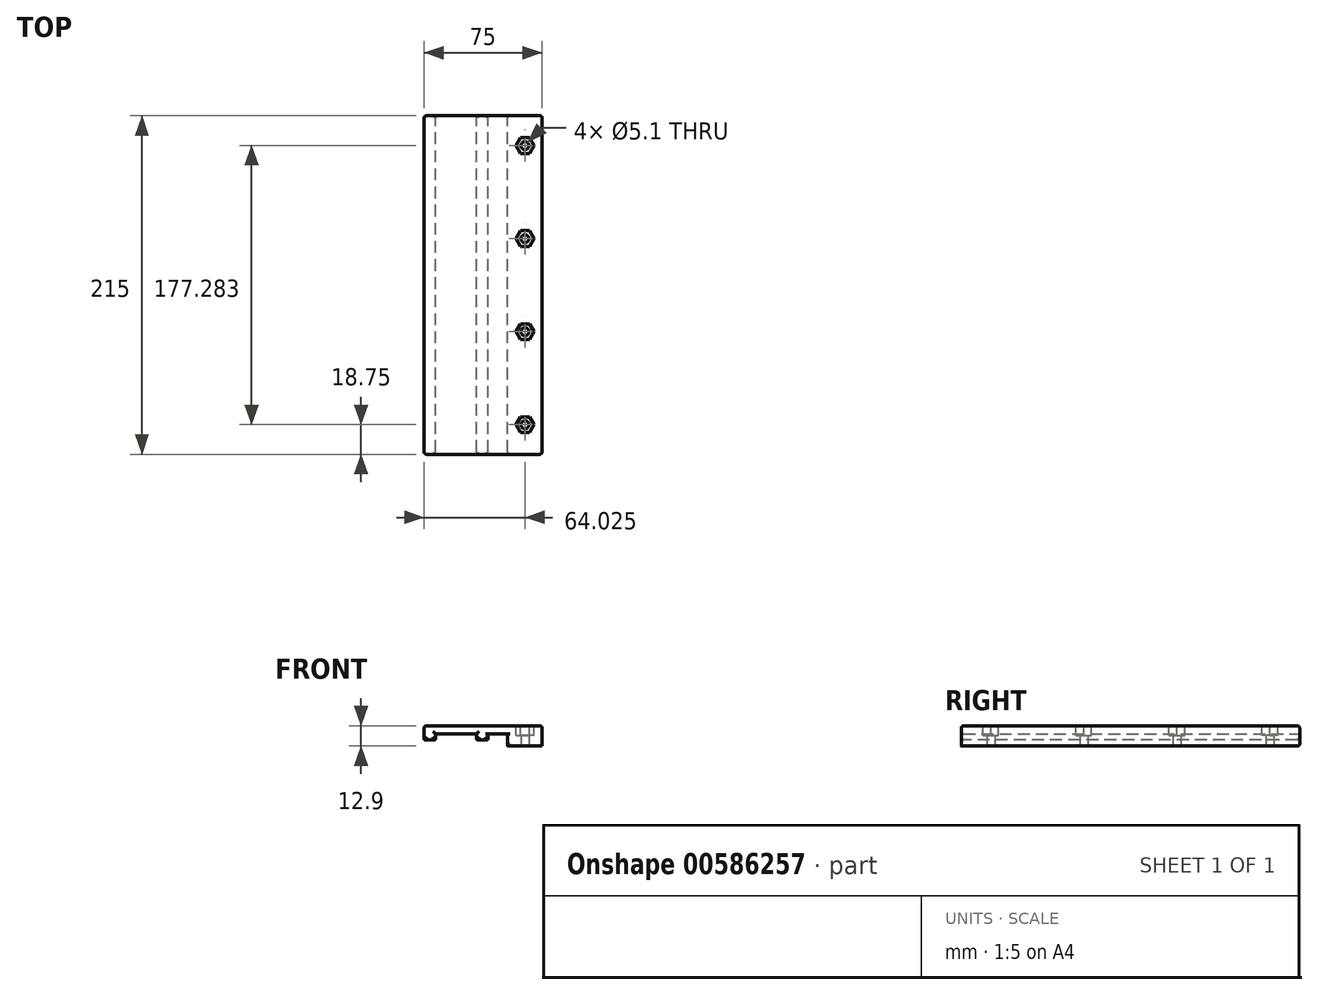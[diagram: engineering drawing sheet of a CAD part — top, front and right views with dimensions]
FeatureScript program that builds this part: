
annotation { "Feature Type Name" : "Feature", "Feature Type Description" : "" }
export const myFeature = defineFeature(function(context is Context, id is Id, definition is map)
    precondition{}
    {
        {
            var Q0;
            Q0=qCreatedBy(makeId("Top.planeOp"),FACE);
            var sketch = newSketch(context, id + "F0", { "sketchPlane" : qUnion([Q0])});
            skLineSegment(sketch, "E0.bottom", {"start": v(37.5, 107.5) * mm, "end": v(-37.5, 107.5) * mm});
            skLineSegment(sketch, "E0.top", {"start": v(37.5, -107.5) * mm, "end": v(-37.5, -107.5) * mm});
            skLineSegment(sketch, "E0.left", {"start": v(37.5, 107.5) * mm, "end": v(37.5, -107.5) * mm});
            skLineSegment(sketch, "E0.right", {"start": v(-37.5, 107.5) * mm, "end": v(-37.5, -107.5) * mm});
            skPoint(sketch, "E0.middle", {"position": v(0, 0) * mm});
            skSolve(sketch);
        }
        {
            var Q0;
            Q0=makeQuery(id+"F0.imprint","IMPRINT",FACE,{"disambiguationData":[TD([[makeQuery(id+"F0.imprint","IMPRINT",EDGE,{"derivedFrom":sQuery(id+"F0.wireOp",EDGE,"E0.bottom")}),1.0]])]});
            extrude(context, id + "F1", {"entities" : qUnion([Q0]), "depth" : 5 * mm, "offsetDistance" : 25 * mm});
        }
        {
            var Q0;
            Q0=makeQuery(id+"F1.opExtrude","CAP_FACE",FACE,{"disambiguationData":[OSD([sQuery(id+"F0.wireOp",EDGE,"E0.bottom"),sQuery(id+"F0.wireOp",EDGE,"E0.top"),sQuery(id+"F0.wireOp",EDGE,"E0.left"),sQuery(id+"F0.wireOp",EDGE,"E0.right")])],"isStart":true});
            var sketch = newSketch(context, id + "F2", { "sketchPlane" : qUnion([Q0])});
            skLineSegment(sketch, "E1.bottom", {"start": v(-37.5, 107.5) * mm, "end": v(-30.3, 107.5) * mm});
            skLineSegment(sketch, "E1.top", {"start": v(-37.5, -107.5) * mm, "end": v(-30.3, -107.5) * mm});
            skLineSegment(sketch, "E1.left", {"start": v(-37.5, 107.5) * mm, "end": v(-37.5, -107.5) * mm});
            skLineSegment(sketch, "E1.right", {"start": v(-30.3, 107.5) * mm, "end": v(-30.3, -107.5) * mm});
            skLineSegment(sketch, "E2.bottom", {"start": v(-4.15, 107.5) * mm, "end": v(3.05, 107.5) * mm});
            skLineSegment(sketch, "E2.top", {"start": v(-4.15, -107.5) * mm, "end": v(3.05, -107.5) * mm});
            skLineSegment(sketch, "E2.left", {"start": v(-4.15, 107.5) * mm, "end": v(-4.15, -107.5) * mm});
            skLineSegment(sketch, "E2.right", {"start": v(3.05, 107.5) * mm, "end": v(3.05, -107.5) * mm});
            skSolve(sketch);
        }
        {
            var Q0;
            Q0=makeQuery(id+"F2.imprint","IMPRINT",FACE,{"disambiguationData":[TD([[makeQuery(id+"F2.imprint","IMPRINT",EDGE,{"derivedFrom":sQuery(id+"F2.wireOp",EDGE,"E1.bottom")}),1.0]])]});
            var Q1;
            Q1=makeQuery(id+"F2.imprint","IMPRINT",FACE,{"disambiguationData":[TD([[makeQuery(id+"F2.imprint","IMPRINT",EDGE,{"derivedFrom":sQuery(id+"F2.wireOp",EDGE,"E2.bottom")}),1.0]])]});
            extrude(context, id + "F3", {"entities" : qUnion([Q0, Q1]), "operationType" : NewBodyOperationType.ADD, "depth" : 4 * mm, "offsetDistance" : 25 * mm});
        }
        {
            var Q0;
            {var subQ0=sQuery(id+"F0.wireOp",EDGE,"E0.left");var subQ1=sQuery(id+"F0.wireOp",EDGE,"E0.top");var subQ2=sQuery(id+"F0.wireOp",EDGE,"E0.bottom");Q0=makeQuery(id+"F3.boolean.opBoolean","SPLIT",FACE,{"disambiguationData":[TD([makeQuery(id+"F1.opExtrude","SWEPT_FACE",FACE,{"disambiguationData":[OSD([subQ0])]})])],"derivedFrom":makeQuery(id+"F1.opExtrude","CAP_FACE",FACE,{"disambiguationData":[OSD([subQ2,subQ1,subQ0,sQuery(id+"F0.wireOp",EDGE,"E0.right")])],"isStart":true})});}
            var sketch = newSketch(context, id + "F4", { "sketchPlane" : qUnion([Q0])});
            skLineSegment(sketch, "E3.bottom", {"start": v(37.5, 107.5) * mm, "end": v(15.55, 107.5) * mm});
            skLineSegment(sketch, "E3.top", {"start": v(37.5, -107.5) * mm, "end": v(15.55, -107.5) * mm});
            skLineSegment(sketch, "E3.left", {"start": v(37.5, 107.5) * mm, "end": v(37.5, -107.5) * mm});
            skLineSegment(sketch, "E3.right", {"start": v(15.55, 107.5) * mm, "end": v(15.55, -107.5) * mm});
            skSolve(sketch);
        }
        {
            var Q0;
            Q0=makeQuery(id+"F4.imprint","IMPRINT",FACE,{"disambiguationData":[TD([[makeQuery(id+"F4.imprint","IMPRINT",EDGE,{"derivedFrom":sQuery(id+"F4.wireOp",EDGE,"E3.bottom")}),1.0]])]});
            extrude(context, id + "F5", {"entities" : qUnion([Q0]), "operationType" : NewBodyOperationType.ADD, "depth" : 7.9 * mm, "offsetDistance" : 25 * mm});
        }
        {
            var Q0;
            Q0=makeQuery(id+"F5.opExtrude","CAP_FACE",FACE,{"disambiguationData":[OSD([sQuery(id+"F4.wireOp",EDGE,"E3.bottom"),sQuery(id+"F4.wireOp",EDGE,"E3.top"),sQuery(id+"F4.wireOp",EDGE,"E3.left"),sQuery(id+"F4.wireOp",EDGE,"E3.right")])],"isStart":false});
            var sketch = newSketch(context, id + "F6", { "sketchPlane" : qUnion([Q0])});
            skCircle(sketch, "E4", {"center": v(26.53, 88.75) * mm, "radius": 2.55 * mm});
            skCircle(sketch, "E5", {"center": v(26.53, 29.66) * mm, "radius": 2.55 * mm});
            skCircle(sketch, "E6", {"center": v(26.53, -29.44) * mm, "radius": 2.55 * mm});
            skCircle(sketch, "E7", {"center": v(26.53, -88.53) * mm, "radius": 2.55 * mm});
            skPoint(sketch, "E8", {"position": v(26.53, 107.5) * mm});
            skPoint(sketch, "E9", {"position": v(26.53, -107.5) * mm});
            skLineSegment(sketch, "E10", {"start": v(26.53, 107.5) * mm, "end": v(26.53, 88.75) * mm, "construction": true});
            skLineSegment(sketch, "E11", {"start": v(26.53, 88.75) * mm, "end": v(26.53, 29.66) * mm, "construction": true});
            skLineSegment(sketch, "E12", {"start": v(26.53, 29.66) * mm, "end": v(26.53, -29.44) * mm, "construction": true});
            skLineSegment(sketch, "E13", {"start": v(26.53, -29.44) * mm, "end": v(26.53, -88.53) * mm, "construction": true});
            skLineSegment(sketch, "E14", {"start": v(26.53, -88.53) * mm, "end": v(26.53, -107.5) * mm, "construction": true});
            skSolve(sketch);
        }
        {
            var Q0;
            Q0=makeQuery(id+"F6.imprint","IMPRINT",FACE,{"disambiguationData":[TD([[makeQuery(id+"F6.imprint","IMPRINT",EDGE,{"derivedFrom":sQuery(id+"F6.wireOp",EDGE,"E4")}),1.0]])]});
            var Q1;
            Q1=makeQuery(id+"F6.imprint","IMPRINT",FACE,{"disambiguationData":[TD([[makeQuery(id+"F6.imprint","IMPRINT",EDGE,{"derivedFrom":sQuery(id+"F6.wireOp",EDGE,"E5")}),1.0]])]});
            var Q2;
            Q2=makeQuery(id+"F6.imprint","IMPRINT",FACE,{"disambiguationData":[TD([[makeQuery(id+"F6.imprint","IMPRINT",EDGE,{"derivedFrom":sQuery(id+"F6.wireOp",EDGE,"E6")}),1.0]])]});
            var Q3;
            Q3=makeQuery(id+"F6.imprint","IMPRINT",FACE,{"disambiguationData":[TD([[makeQuery(id+"F6.imprint","IMPRINT",EDGE,{"derivedFrom":sQuery(id+"F6.wireOp",EDGE,"E7")}),1.0]])]});
            var Q4;
            Q4=makeQuery(id+"F1.opExtrude","CAP_FACE",FACE,{"disambiguationData":[OSD([sQuery(id+"F0.wireOp",EDGE,"E0.bottom"),sQuery(id+"F0.wireOp",EDGE,"E0.top"),sQuery(id+"F0.wireOp",EDGE,"E0.left"),sQuery(id+"F0.wireOp",EDGE,"E0.right")])],"isStart":false});
            extrude(context, id + "F7", {"entities" : qUnion([Q0, Q1, Q2, Q3]), "operationType" : NewBodyOperationType.REMOVE, "endBound" : BoundingType.UP_TO_SURFACE, "oppositeDirection" : true, "depth" : 25 * mm, "endBoundEntityFace" : qUnion([Q4]), "offsetDistance" : 25 * mm});
        }
        {
            var Q0;
            Q0=makeQuery(id+"F3.opExtrude","SWEPT_EDGE",EDGE,{"disambiguationData":[OSD([sQuery(id+"F0.wireOp",EDGE,"E0.bottom"),sQuery(id+"F2.wireOp",EDGE,"E1.top"),sQuery(id+"F2.wireOp",EDGE,"E1.right")])]});
            var Q1;
            Q1=makeQuery(id+"F3.opExtrude","CAP_EDGE",EDGE,{"disambiguationData":[OSD([sQuery(id+"F2.wireOp",EDGE,"E1.top")])],"isStart":false});
            var Q2;
            Q2=makeQuery(id+"F3.boolean.opBoolean","MERGE",EDGE,{"derivedFrom":[makeQuery(id+"F1.opExtrude","SWEPT_EDGE",EDGE,{"disambiguationData":[OSD([sQuery(id+"F0.wireOp",EDGE,"E0.bottom"),sQuery(id+"F0.wireOp",EDGE,"E0.right")])]}),makeQuery(id+"F3.opExtrude","SWEPT_EDGE",EDGE,{"disambiguationData":[OSD([sQuery(id+"F2.wireOp",EDGE,"E1.top"),sQuery(id+"F2.wireOp",EDGE,"E1.left")])]})]});
            var Q3;
            Q3=makeQuery(id+"F3.opExtrude","SWEPT_EDGE",EDGE,{"disambiguationData":[OSD([sQuery(id+"F0.wireOp",EDGE,"E0.bottom"),sQuery(id+"F2.wireOp",EDGE,"E2.top"),sQuery(id+"F2.wireOp",EDGE,"E2.left")])]});
            var Q4;
            Q4=makeQuery(id+"F3.opExtrude","CAP_EDGE",EDGE,{"disambiguationData":[OSD([sQuery(id+"F2.wireOp",EDGE,"E2.top")])],"isStart":false});
            var Q5;
            Q5=makeQuery(id+"F3.opExtrude","SWEPT_EDGE",EDGE,{"disambiguationData":[OSD([sQuery(id+"F0.wireOp",EDGE,"E0.bottom"),sQuery(id+"F2.wireOp",EDGE,"E2.top"),sQuery(id+"F2.wireOp",EDGE,"E2.right")])]});
            var Q6;
            Q6=makeQuery(id+"F5.opExtrude","SWEPT_EDGE",EDGE,{"disambiguationData":[OSD([sQuery(id+"F0.wireOp",EDGE,"E0.bottom"),sQuery(id+"F4.wireOp",EDGE,"E3.top"),sQuery(id+"F4.wireOp",EDGE,"E3.right")])]});
            var Q7;
            Q7=makeQuery(id+"F5.boolean.opBoolean","MERGE",EDGE,{"derivedFrom":[makeQuery(id+"F1.opExtrude","SWEPT_EDGE",EDGE,{"disambiguationData":[OSD([sQuery(id+"F0.wireOp",EDGE,"E0.bottom"),sQuery(id+"F0.wireOp",EDGE,"E0.left")])]}),makeQuery(id+"F5.opExtrude","SWEPT_EDGE",EDGE,{"disambiguationData":[OSD([sQuery(id+"F4.wireOp",EDGE,"E3.top"),sQuery(id+"F4.wireOp",EDGE,"E3.left")])]})]});
            var Q8;
            Q8=makeQuery(id+"F5.opExtrude","CAP_EDGE",EDGE,{"disambiguationData":[OSD([sQuery(id+"F4.wireOp",EDGE,"E3.top")])],"isStart":false});
            var Q9;
            Q9=makeQuery(id+"F5.opExtrude","SWEPT_EDGE",EDGE,{"disambiguationData":[OSD([sQuery(id+"F0.wireOp",EDGE,"E0.top"),sQuery(id+"F4.wireOp",EDGE,"E3.bottom"),sQuery(id+"F4.wireOp",EDGE,"E3.right")])]});
            var Q10;
            Q10=makeQuery(id+"F3.opExtrude","SWEPT_EDGE",EDGE,{"disambiguationData":[OSD([sQuery(id+"F0.wireOp",EDGE,"E0.top"),sQuery(id+"F2.wireOp",EDGE,"E2.bottom"),sQuery(id+"F2.wireOp",EDGE,"E2.right")])]});
            var Q11;
            Q11=makeQuery(id+"F3.opExtrude","SWEPT_EDGE",EDGE,{"disambiguationData":[OSD([sQuery(id+"F0.wireOp",EDGE,"E0.top"),sQuery(id+"F2.wireOp",EDGE,"E2.bottom"),sQuery(id+"F2.wireOp",EDGE,"E2.left")])]});
            var Q12;
            Q12=makeQuery(id+"F3.opExtrude","SWEPT_EDGE",EDGE,{"disambiguationData":[OSD([sQuery(id+"F0.wireOp",EDGE,"E0.top"),sQuery(id+"F2.wireOp",EDGE,"E1.bottom"),sQuery(id+"F2.wireOp",EDGE,"E1.right")])]});
            var Q13;
            {var subQ0=sQuery(id+"F0.wireOp",EDGE,"E0.top");Q13=makeQuery(id+"F3.boolean.opBoolean","SPLIT",EDGE,{"disambiguationData":[TD([makeQuery(id+"F3.opExtrude","SWEPT_FACE",FACE,{"disambiguationData":[OSD([sQuery(id+"F2.wireOp",EDGE,"E1.right")])]})])],"derivedFrom":makeQuery(id+"F1.opExtrude","CAP_EDGE",EDGE,{"disambiguationData":[OSD([subQ0])],"isStart":true})});}
            var Q14;
            Q14=makeQuery(id+"F3.boolean.opBoolean","MERGE",EDGE,{"derivedFrom":[makeQuery(id+"F1.opExtrude","SWEPT_EDGE",EDGE,{"disambiguationData":[OSD([sQuery(id+"F0.wireOp",EDGE,"E0.top"),sQuery(id+"F0.wireOp",EDGE,"E0.right")])]}),makeQuery(id+"F3.opExtrude","SWEPT_EDGE",EDGE,{"disambiguationData":[OSD([sQuery(id+"F2.wireOp",EDGE,"E1.bottom"),sQuery(id+"F2.wireOp",EDGE,"E1.left")])]})]});
            var Q15;
            Q15=makeQuery(id+"F3.opExtrude","CAP_EDGE",EDGE,{"disambiguationData":[OSD([sQuery(id+"F2.wireOp",EDGE,"E2.bottom")])],"isStart":false});
            var Q16;
            Q16=makeQuery(id+"F3.opExtrude","CAP_EDGE",EDGE,{"disambiguationData":[OSD([sQuery(id+"F2.wireOp",EDGE,"E1.bottom")])],"isStart":false});
            var Q17;
            Q17=makeQuery(id+"F1.opExtrude","CAP_EDGE",EDGE,{"disambiguationData":[OSD([sQuery(id+"F0.wireOp",EDGE,"E0.left")])],"isStart":false});
            var Q18;
            Q18=makeQuery(id+"F1.opExtrude","CAP_EDGE",EDGE,{"disambiguationData":[OSD([sQuery(id+"F0.wireOp",EDGE,"E0.right")])],"isStart":false});
            var Q19;
            Q19=makeQuery(id+"F1.opExtrude","CAP_EDGE",EDGE,{"disambiguationData":[OSD([sQuery(id+"F0.wireOp",EDGE,"E0.bottom")])],"isStart":false});
            var Q20;
            Q20=makeQuery(id+"F1.opExtrude","CAP_EDGE",EDGE,{"disambiguationData":[OSD([sQuery(id+"F0.wireOp",EDGE,"E0.top")])],"isStart":false});
            var Q21;
            Q21=makeQuery(id+"F5.boolean.opBoolean","MERGE",EDGE,{"derivedFrom":[makeQuery(id+"F1.opExtrude","SWEPT_EDGE",EDGE,{"disambiguationData":[OSD([sQuery(id+"F0.wireOp",EDGE,"E0.top"),sQuery(id+"F0.wireOp",EDGE,"E0.left")])]}),makeQuery(id+"F5.opExtrude","SWEPT_EDGE",EDGE,{"disambiguationData":[OSD([sQuery(id+"F4.wireOp",EDGE,"E3.bottom"),sQuery(id+"F4.wireOp",EDGE,"E3.left")])]})]});
            fillet(context, id + "F8", {"entities" : qUnion([Q0, Q1, Q2, Q3, Q4, Q5, Q6, Q7, Q8, Q9, Q10, Q11, Q12, Q13, Q14, Q15, Q16, Q17, Q18, Q19, Q20, Q21]), "radius" : 1.5 * mm, "tangentPropagation" : true, "allowEdgeOverflow" : false});
        }
        {
            var Q0;
            Q0=makeQuery(id+"F3.opExtrude","CAP_EDGE",EDGE,{"disambiguationData":[OSD([sQuery(id+"F2.wireOp",EDGE,"E1.right")])],"isStart":false});
            var Q1;
            Q1=makeQuery(id+"F3.opExtrude","CAP_EDGE",EDGE,{"disambiguationData":[OSD([sQuery(id+"F2.wireOp",EDGE,"E2.left")])],"isStart":false});
            var Q2;
            Q2=makeQuery(id+"F3.opExtrude","CAP_EDGE",EDGE,{"disambiguationData":[OSD([sQuery(id+"F2.wireOp",EDGE,"E2.right")])],"isStart":false});
            var Q3;
            Q3=makeQuery(id+"F3.opExtrude","CAP_EDGE",EDGE,{"disambiguationData":[OSD([sQuery(id+"F2.wireOp",EDGE,"E1.left")])],"isStart":false});
            fillet(context, id + "F9", {"entities" : qUnion([Q0, Q1, Q2, Q3]), "radius" : .7 * mm, "tangentPropagation" : true, "allowEdgeOverflow" : false});
        }
        {
            var Q0;
            Q0=makeQuery(id+"F1.opExtrude","CAP_FACE",FACE,{"disambiguationData":[OSD([sQuery(id+"F0.wireOp",EDGE,"E0.bottom"),sQuery(id+"F0.wireOp",EDGE,"E0.top"),sQuery(id+"F0.wireOp",EDGE,"E0.left"),sQuery(id+"F0.wireOp",EDGE,"E0.right")])],"isStart":false});
            var sketch = newSketch(context, id + "F10", { "sketchPlane" : qUnion([Q0])});
            skCircle(sketch, "E15.cCircle", {"center": v(26.53, 88.53) * mm, "radius": 5 * mm, "construction": true});
            skLineSegment(sketch, "E15.0", {"start": v(29.41, 83.53) * mm, "end": v(23.64, 83.53) * mm});
            skLineSegment(sketch, "E15.1", {"start": v(23.64, 83.53) * mm, "end": v(20.75, 88.53) * mm});
            skLineSegment(sketch, "E15.2", {"start": v(20.75, 88.53) * mm, "end": v(23.64, 93.53) * mm});
            skLineSegment(sketch, "E15.3", {"start": v(23.64, 93.53) * mm, "end": v(29.41, 93.53) * mm});
            skLineSegment(sketch, "E15.4", {"start": v(29.41, 93.53) * mm, "end": v(32.3, 88.53) * mm});
            skLineSegment(sketch, "E15.5", {"start": v(32.3, 88.53) * mm, "end": v(29.41, 83.53) * mm});
            skPoint(sketch, "E15.0.midPoint", {"position": v(26.53, 83.53) * mm});
            skCircle(sketch, "E16.cCircle", {"center": v(26.53, 29.44) * mm, "radius": 5 * mm, "construction": true});
            skLineSegment(sketch, "E16.0", {"start": v(23.64, 34.44) * mm, "end": v(29.41, 34.44) * mm});
            skLineSegment(sketch, "E16.1", {"start": v(29.41, 34.44) * mm, "end": v(32.3, 29.44) * mm});
            skLineSegment(sketch, "E16.2", {"start": v(32.3, 29.44) * mm, "end": v(29.41, 24.44) * mm});
            skLineSegment(sketch, "E16.3", {"start": v(29.41, 24.44) * mm, "end": v(23.64, 24.44) * mm});
            skLineSegment(sketch, "E16.4", {"start": v(23.64, 24.44) * mm, "end": v(20.75, 29.44) * mm});
            skLineSegment(sketch, "E16.5", {"start": v(20.75, 29.44) * mm, "end": v(23.64, 34.44) * mm});
            skPoint(sketch, "E16.0.midPoint", {"position": v(26.53, 34.44) * mm});
            skCircle(sketch, "E17.cCircle", {"center": v(26.53, -29.66) * mm, "radius": 5 * mm, "construction": true});
            skLineSegment(sketch, "E17.0", {"start": v(23.64, -24.66) * mm, "end": v(29.41, -24.66) * mm});
            skLineSegment(sketch, "E17.1", {"start": v(29.41, -24.66) * mm, "end": v(32.3, -29.66) * mm});
            skLineSegment(sketch, "E17.2", {"start": v(32.3, -29.66) * mm, "end": v(29.41, -34.66) * mm});
            skLineSegment(sketch, "E17.3", {"start": v(29.41, -34.66) * mm, "end": v(23.64, -34.66) * mm});
            skLineSegment(sketch, "E17.4", {"start": v(23.64, -34.66) * mm, "end": v(20.75, -29.66) * mm});
            skLineSegment(sketch, "E17.5", {"start": v(20.75, -29.66) * mm, "end": v(23.64, -24.66) * mm});
            skPoint(sketch, "E17.0.midPoint", {"position": v(26.53, -24.66) * mm});
            skCircle(sketch, "E18.cCircle", {"center": v(26.53, -88.75) * mm, "radius": 5 * mm, "construction": true});
            skLineSegment(sketch, "E18.0", {"start": v(23.64, -83.75) * mm, "end": v(29.41, -83.75) * mm});
            skLineSegment(sketch, "E18.1", {"start": v(29.41, -83.75) * mm, "end": v(32.3, -88.75) * mm});
            skLineSegment(sketch, "E18.2", {"start": v(32.3, -88.75) * mm, "end": v(29.41, -93.75) * mm});
            skLineSegment(sketch, "E18.3", {"start": v(29.41, -93.75) * mm, "end": v(23.64, -93.75) * mm});
            skLineSegment(sketch, "E18.4", {"start": v(23.64, -93.75) * mm, "end": v(20.75, -88.75) * mm});
            skLineSegment(sketch, "E18.5", {"start": v(20.75, -88.75) * mm, "end": v(23.64, -83.75) * mm});
            skPoint(sketch, "E18.0.midPoint", {"position": v(26.53, -83.75) * mm});
            skSolve(sketch);
        }
        {
            var Q0;
            Q0=makeQuery(id+"F10.imprint","IMPRINT",FACE,{"disambiguationData":[TD([[makeQuery(id+"F10.imprint","IMPRINT",EDGE,{"derivedFrom":sQuery(id+"F10.wireOp",EDGE,"E16.0")}),-1.0]])]});
            var Q1;
            Q1=makeQuery(id+"F10.imprint","IMPRINT",FACE,{"disambiguationData":[TD([[makeQuery(id+"F10.imprint","IMPRINT",EDGE,{"derivedFrom":sQuery(id+"F10.wireOp",EDGE,"E17.0")}),-1.0]])]});
            var Q2;
            Q2=makeQuery(id+"F10.imprint","IMPRINT",FACE,{"disambiguationData":[TD([[makeQuery(id+"F10.imprint","IMPRINT",EDGE,{"derivedFrom":sQuery(id+"F10.wireOp",EDGE,"E18.0")}),-1.0]])]});
            var Q3;
            Q3=makeQuery(id+"F10.imprint","IMPRINT",FACE,{"disambiguationData":[TD([[makeQuery(id+"F10.imprint","IMPRINT",EDGE,{"derivedFrom":sQuery(id+"F10.wireOp",EDGE,"E15.0")}),-1.0]])]});
            extrude(context, id + "F11", {"entities" : qUnion([Q0, Q1, Q2, Q3]), "operationType" : NewBodyOperationType.REMOVE, "oppositeDirection" : true, "depth" : 6 * mm, "offsetDistance" : 25 * mm});
        }
    });
